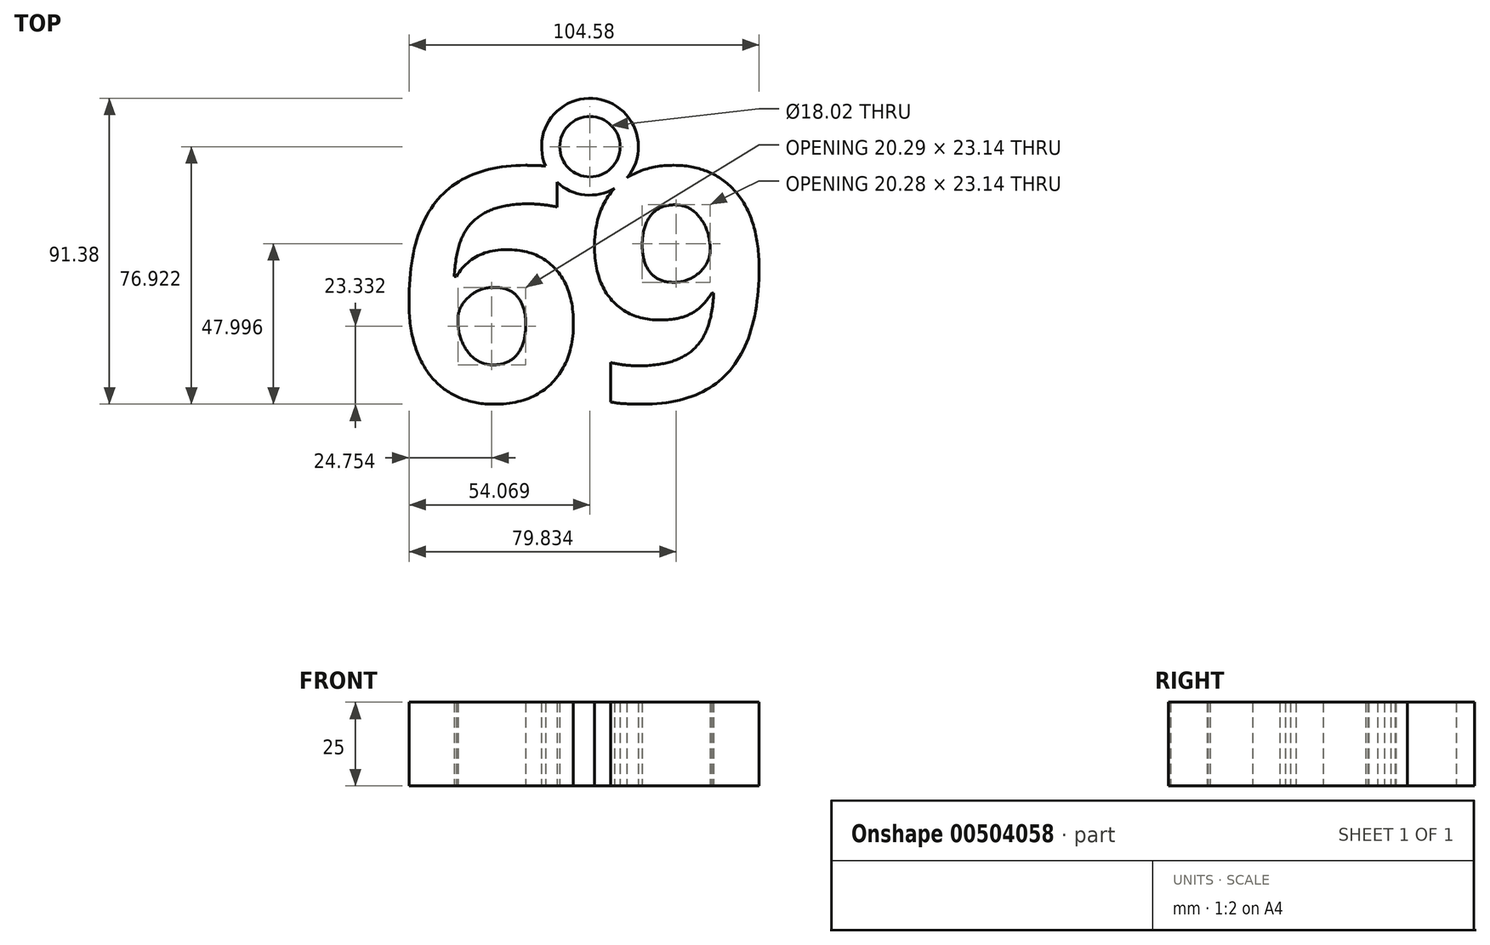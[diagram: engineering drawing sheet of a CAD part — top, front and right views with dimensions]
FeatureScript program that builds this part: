
annotation { "Feature Type Name" : "Feature", "Feature Type Description" : "" }
export const myFeature = defineFeature(function(context is Context, id is Id, definition is map)
    precondition{}
    {
        {
            var Q0;
            Q0=qCreatedBy(makeId("Top.planeOp"),FACE);
            var sketch = newSketch(context, id + "F0", { "sketchPlane" : qUnion([Q0])});
            skText(sketch, "E0", { "text": "69", "fontName": "NotoSans-Bold.ttf"});
            skCircle(sketch, "E1", {"center": v(4.04, 37.21) * mm, "radius": 14.46 * mm});
            skCircle(sketch, "E2", {"center": v(4.04, 37.21) * mm, "radius": 9.01 * mm});
            const initialGuessF0  = {"E0": [-0.05346, -0.03875, 1, 0, 0.0702]};
            skSetInitialGuess(sketch, initialGuessF0);
            skSolve(sketch);
        }
        {
            var Q0;
            Q0 = qSketchRegion(id + "F0", true);
            extrude(context, id + "F1", {"entities" : qUnion([Q0]), "depth" : 25 * mm});
        }
    });
